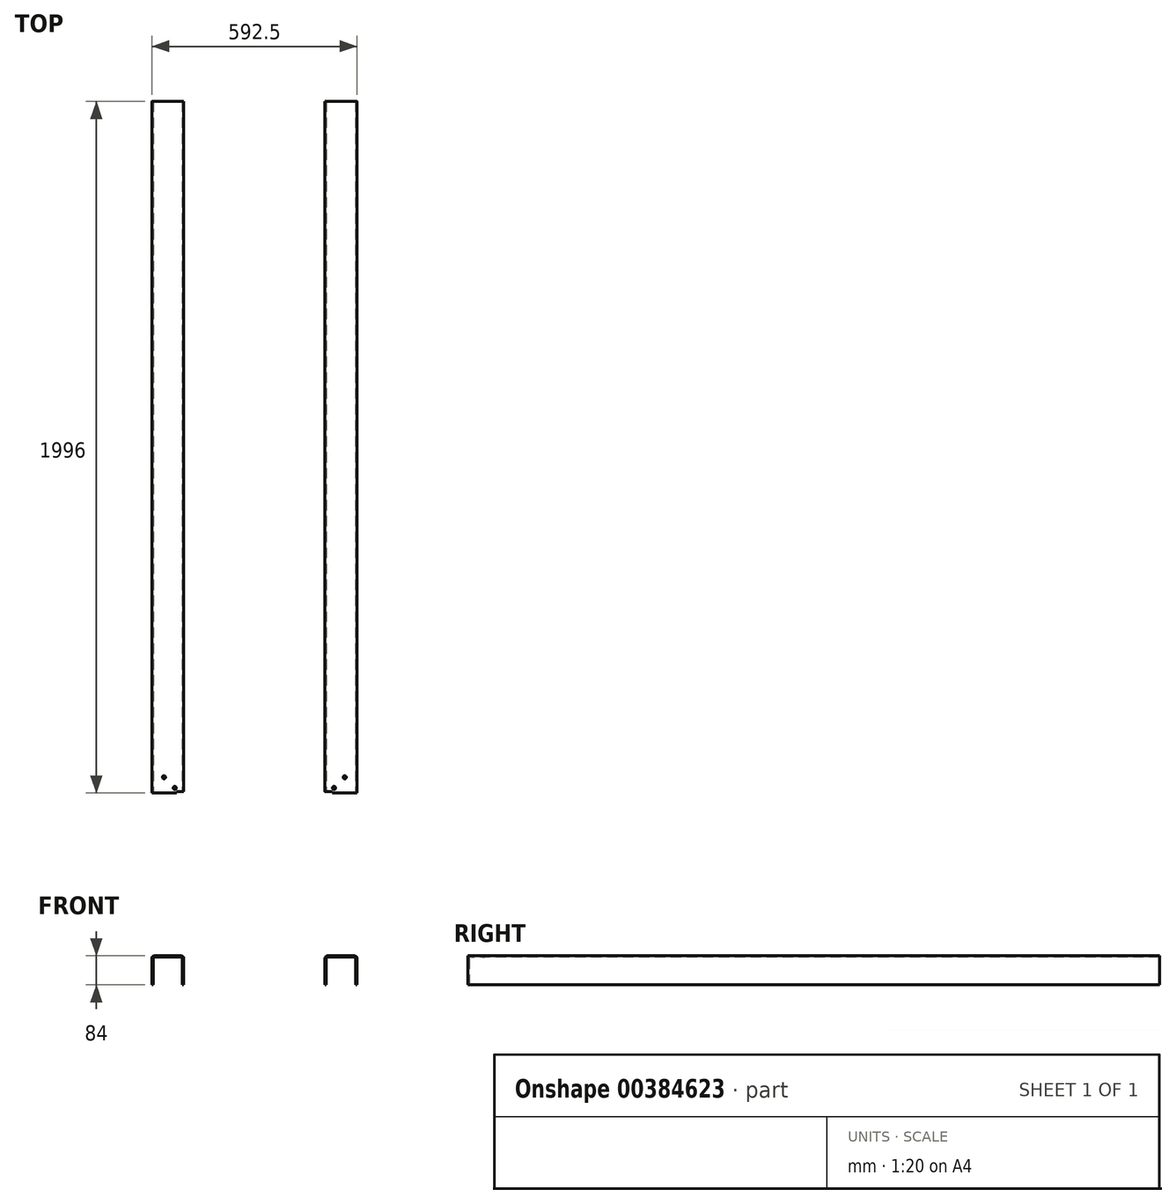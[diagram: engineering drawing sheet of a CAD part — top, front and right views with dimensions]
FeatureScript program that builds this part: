
annotation { "Feature Type Name" : "Feature", "Feature Type Description" : "" }
export const myFeature = defineFeature(function(context is Context, id is Id, definition is map)
    precondition{}
    {
        {
            var Q0;
            Q0=qCreatedBy(makeId("Front.planeOp"),FACE);
            var sketch = newSketch(context, id + "F0", { "sketchPlane" : qUnion([Q0])});
            skLineSegment(sketch, "E0.bottom", {"start": v(-46.25, -42) * mm, "end": v(-42.25, -42) * mm});
            skLineSegment(sketch, "E0.top", {"start": v(-38.25, 42) * mm, "end": v(38.25, 42) * mm});
            skLineSegment(sketch, "E0.left", {"start": v(-46.25, -42) * mm, "end": v(-46.25, 34) * mm});
            skLineSegment(sketch, "E0.right", {"start": v(46.25, -42) * mm, "end": v(46.25, 34) * mm});
            skPoint(sketch, "E0.middle", {"position": v(0, 0) * mm});
            skLineSegment(sketch, "E1", {"start": v(-42.25, -42) * mm, "end": v(-42.25, 34) * mm});
            skLineSegment(sketch, "E2", {"start": v(-38.25, 38) * mm, "end": v(38.25, 38) * mm});
            skLineSegment(sketch, "E3", {"start": v(42.25, 34) * mm, "end": v(42.25, -42) * mm});
            skLineSegment(sketch, "E4.trimOffspring", {"start": v(42.25, -42) * mm, "end": v(46.25, -42) * mm});
            skPoint(sketch, "E5.visualSharp", {"position": v(-42.25, 38) * mm});
            skArc(sketch, "E5.filletArc", {"start": v(-38.25, 38) * mm, "mid": v(-41.08, 36.83) * mm, "end": v(-42.25, 34) * mm});
            skPoint(sketch, "E6.visualSharp", {"position": v(42.25, 38) * mm});
            skArc(sketch, "E6.filletArc", {"start": v(42.25, 34) * mm, "mid": v(41.08, 36.83) * mm, "end": v(38.25, 38) * mm});
            skPoint(sketch, "E7.visualSharp", {"position": v(-46.25, 42) * mm});
            skArc(sketch, "E7.filletArc", {"start": v(-38.25, 42) * mm, "mid": v(-43.9, 39.66) * mm, "end": v(-46.25, 34) * mm});
            skPoint(sketch, "E8.visualSharp", {"position": v(46.25, 42) * mm});
            skArc(sketch, "E8.filletArc", {"start": v(46.25, 34) * mm, "mid": v(43.9, 39.66) * mm, "end": v(38.25, 42) * mm});
            skSolve(sketch);
        }
        {
            var Q0;
            Q0=makeQuery(id+"F0.imprint","IMPRINT",FACE,{"disambiguationData":[TD([[makeQuery(id+"F0.imprint","IMPRINT",EDGE,{"derivedFrom":sQuery(id+"F0.wireOp",EDGE,"E0.bottom")}),1.0]])]});
            extrude(context, id + "F1", {"entities" : qUnion([Q0]), "oppositeDirection" : true, "depth" : 1996 * mm});
        }
        {
            var Q0;
            Q0=qCreatedBy(makeId("Right.planeOp"),FACE);
            var Q1;
            Q1=makeQuery(id+"F1.opExtrude","CAP_EDGE",EDGE,{"disambiguationData":[OSD([sQuery(id+"F0.wireOp",EDGE,"E0.left")])],"isStart":true});
            cPlane(context, id + "F2", {"entities" : qUnion([Q0, Q1]), "cplaneType" : CPlaneType.LINE_ANGLE, "offset" : 25 * mm, "angle" : 0 * degree, "width" : 150 * mm, "height" : 150 * mm});
        }
        {
            var Q0;
            Q0=qCreatedBy(id+"F2.planeOp",FACE);
            var sketch = newSketch(context, id + "F3", { "sketchPlane" : qUnion([Q0])});
            skLineSegment(sketch, "E9.bottom", {"start": v(0, -43.13) * mm, "end": v(-4, -43.13) * mm});
            skLineSegment(sketch, "E9.top", {"start": v(0, 43.87) * mm, "end": v(-4, 43.87) * mm});
            skLineSegment(sketch, "E9.left", {"start": v(0, -43.13) * mm, "end": v(0, 43.87) * mm});
            skLineSegment(sketch, "E9.right", {"start": v(-4, -43.13) * mm, "end": v(-4, 43.87) * mm});
            skSolve(sketch);
        }
        {
            var Q0;
            Q0=makeQuery(id+"F3.imprint","IMPRINT",FACE,{"disambiguationData":[TD([[makeQuery(id+"F3.imprint","IMPRINT",EDGE,{"derivedFrom":sQuery(id+"F3.wireOp",EDGE,"E9.bottom")}),-1.0]])]});
            extrude(context, id + "F4", {"entities" : qUnion([Q0]), "operationType" : NewBodyOperationType.REMOVE, "oppositeDirection" : true, "depth" : 21.4 * mm});
        }
        {
            var Q0;
            Q0=makeQuery(id+"F1.opExtrude","SWEPT_FACE",FACE,{"disambiguationData":[OSD([sQuery(id+"F0.wireOp",EDGE,"E2")])]});
            var sketch = newSketch(context, id + "F5", { "sketchPlane" : qUnion([Q0])});
            skPoint(sketch, "E10.middle", {"position": v(0, 0) * mm});
            skPoint(sketch, "E10.bottom.end.orphan", {"position": v(-19.52, 14.96) * mm});
            skPoint(sketch, "E10.bottom.start.orphan", {"position": v(19.52, 14.96) * mm});
            skPoint(sketch, "E10.left.end.orphan", {"position": v(19.52, -14.96) * mm});
            skLineSegment(sketch, "E11", {"start": v(-20.12, 0) * mm, "end": v(-20.12, -14.5) * mm});
            skLineSegment(sketch, "E12", {"start": v(-20.12, -14.5) * mm, "end": v(-20.12, -45.5) * mm});
            skLineSegment(sketch, "E13", {"start": v(-20.12, -45.5) * mm, "end": v(10.88, -45.5) * mm});
            skCircle(sketch, "E14", {"center": v(10.88, -45.5) * mm, "radius": 4.5 * mm});
            skCircle(sketch, "E15", {"center": v(-20.12, -14.5) * mm, "radius": 4.5 * mm});
            skLineSegment(sketch, "E16", {"start": v(-20.12, 0) * mm, "end": v(-46.25, 0) * mm});
            skSolve(sketch);
        }
        {
            var Q0;
            Q0=makeQuery(id+"F5.imprint","IMPRINT",FACE,{"disambiguationData":[TD([[makeQuery(id+"F5.imprint","IMPRINT",EDGE,{"derivedFrom":sQuery(id+"F5.wireOp",EDGE,"E14")}),1.0]])]});
            var Q1;
            {var subQ0=sQuery(id+"F5.wireOp",EDGE,"E12");var subQ1=sQuery(id+"F5.wireOp",EDGE,"E11");var subQ2=makeQuery(id+"F5.imprint","INTERSECT",VERTEX,{"derivedFrom":[subQ1,subQ0]});Q1=makeQuery(id+"F5.imprint","IMPRINT",FACE,{"disambiguationData":[TD([[makeQuery(id+"F5.imprint","IMPRINT",EDGE,{"disambiguationData":[TD([[subQ2,1.0]])],"derivedFrom":subQ1}),-1.0]])]});}
            var Q2;
            {var subQ0=sQuery(id+"F5.wireOp",EDGE,"E12");var subQ1=sQuery(id+"F5.wireOp",EDGE,"E11");var subQ2=makeQuery(id+"F5.imprint","INTERSECT",VERTEX,{"derivedFrom":[subQ1,subQ0]});Q2=makeQuery(id+"F5.imprint","IMPRINT",FACE,{"disambiguationData":[TD([[makeQuery(id+"F5.imprint","IMPRINT",EDGE,{"disambiguationData":[TD([[subQ2,1.0]])],"derivedFrom":subQ1}),1.0]])]});}
            extrude(context, id + "F6", {"entities" : qUnion([Q0, Q1, Q2]), "operationType" : NewBodyOperationType.REMOVE, "oppositeDirection" : true, "depth" : 4 * mm});
        }
        {
            var Q0;
            Q0=qCreatedBy(makeId("Right.planeOp"),FACE);
            cPlane(context, id + "F7", {"entities" : qUnion([Q0]), "cplaneType" : CPlaneType.OFFSET, "offset" : 250 * mm, "oppositeDirection" : true, "width" : 150 * mm, "height" : 150 * mm});
        }
        {
            var Q0;
            Q0=makeQuery(id+"F1.opExtrude","SWEPT_BODY",BODY,{"disambiguationData":[OSD([sQuery(id+"F0.wireOp",EDGE,"E0.bottom"),sQuery(id+"F0.wireOp",EDGE,"E0.top"),sQuery(id+"F0.wireOp",EDGE,"E0.left"),sQuery(id+"F0.wireOp",EDGE,"E0.right"),sQuery(id+"F0.wireOp",EDGE,"E1"),sQuery(id+"F0.wireOp",EDGE,"E2"),sQuery(id+"F0.wireOp",EDGE,"E3"),sQuery(id+"F0.wireOp",EDGE,"E4.trimOffspring"),sQuery(id+"F0.wireOp",EDGE,"E5.filletArc"),sQuery(id+"F0.wireOp",EDGE,"E6.filletArc"),sQuery(id+"F0.wireOp",EDGE,"E7.filletArc"),sQuery(id+"F0.wireOp",EDGE,"E8.filletArc")])]});
            var Q1;
            Q1=qCreatedBy(id+"F7.planeOp",FACE);
            mirror(context, id + "F8", {"entities" : qUnion([Q0]), "mirrorPlane" : qUnion([Q1])});
        }
    });
